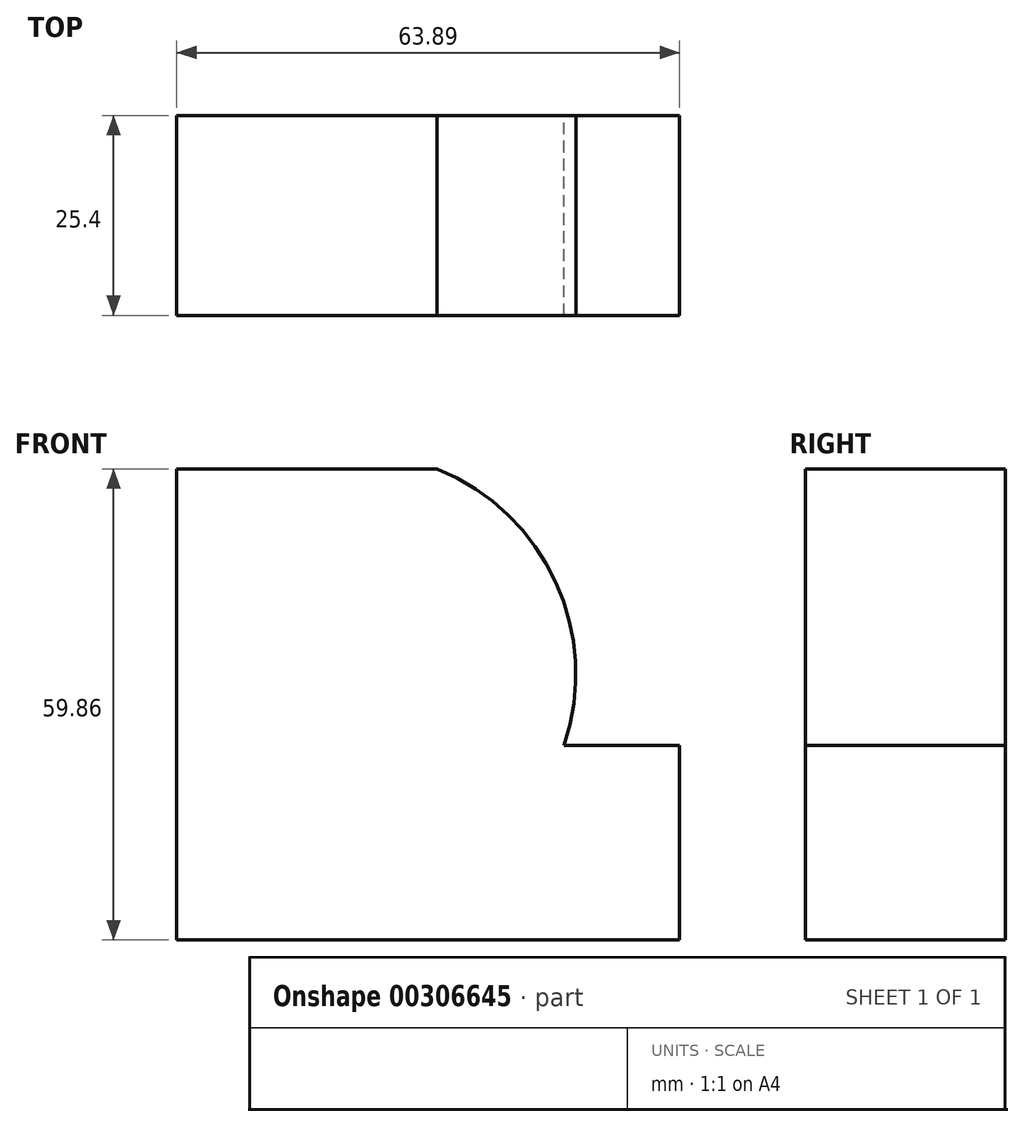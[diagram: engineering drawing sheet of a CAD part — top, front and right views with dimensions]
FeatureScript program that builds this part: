
annotation { "Feature Type Name" : "Feature", "Feature Type Description" : "" }
export const myFeature = defineFeature(function(context is Context, id is Id, definition is map)
    precondition{}
    {
        {
            var Q0;
            Q0=qCreatedBy(makeId("Front.planeOp"),FACE);
            var sketch = newSketch(context, id + "F0", { "sketchPlane" : qUnion([Q0])});
            skLineSegment(sketch, "E0", {"start": v(-30.8, 59.86) * mm, "end": v(-63.9, 59.86) * mm});
            skLineSegment(sketch, "E1", {"start": v(-63.9, 59.86) * mm, "end": v(-63.9, 0) * mm});
            skLineSegment(sketch, "E2", {"start": v(-63.9, 0) * mm, "end": v(0, 0) * mm});
            skLineSegment(sketch, "E3", {"start": v(0, 0) * mm, "end": v(0, 24.74) * mm});
            skLineSegment(sketch, "E4", {"start": v(0, 24.74) * mm, "end": v(-14.67, 24.74) * mm});
            skArc(sketch, "E5", {"start": v(-14.67, 24.74) * mm, "mid": v(-15.76, 45.5) * mm, "end": v(-30.8, 59.86) * mm});
            skSolve(sketch);
        }
        {
            var Q0;
            Q0 = qSketchRegion(id + "F0", true);
            extrude(context, id + "F1", {"entities" : qUnion([Q0]), "depth" : 25.4 * mm});
        }
    });
